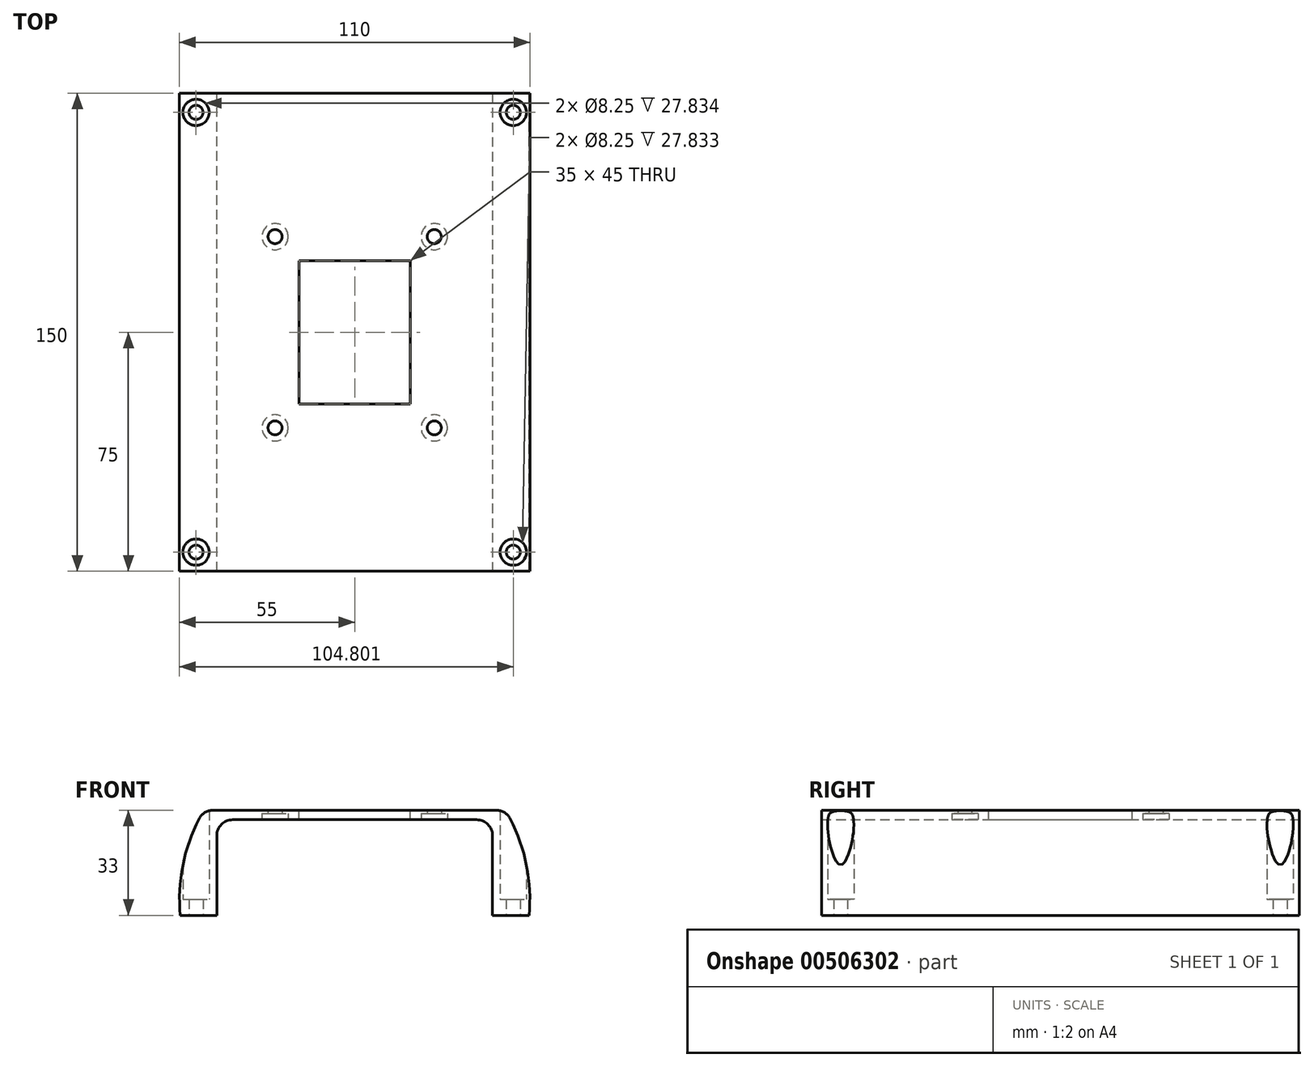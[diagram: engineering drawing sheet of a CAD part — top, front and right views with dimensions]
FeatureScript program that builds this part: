
annotation { "Feature Type Name" : "Feature", "Feature Type Description" : "" }
export const myFeature = defineFeature(function(context is Context, id is Id, definition is map)
    precondition{}
    {
        {
            var Q0;
            Q0=qCreatedBy(makeId("Front.planeOp"),FACE);
            var sketch = newSketch(context, id + "F0", { "sketchPlane" : qUnion([Q0])});
            skCircle(sketch, "E0", {"center": v(0, 0) * mm, "radius": 50 * mm});
            skCircle(sketch, "E1.0", {"center": v(0, 0) * mm, "radius": 55 * mm});
            skSolve(sketch);
        }
        {
            var Q0;
            Q0=qSketchRegion(id+"F0",true);
            extrude(context, id + "F1", {"entities" : qUnion([Q0]), "depth" : 150 * mm});
        }
        {
            var Q0;
            Q0=makeQuery(id+"F1.opExtrude","CAP_FACE",FACE,{"disambiguationData":[OSD([sQuery(id+"F0.wireOp",EDGE,"E0"),sQuery(id+"F0.wireOp",EDGE,"E1.0")])],"isStart":false});
            var sketch = newSketch(context, id + "F2", { "sketchPlane" : qUnion([Q0])});
            skLineSegment(sketch, "E2.bottom", {"start": v(-54.77, -5) * mm, "end": v(54.77, -5) * mm});
            skLineSegment(sketch, "E2.top", {"start": v(-54.08, -10) * mm, "end": v(54.08, -10) * mm});
            skArc(sketch, "E3.0", {"start": v(-54.77, -5) * mm, "mid": v(-54.49, -7.5) * mm, "end": v(-54.08, -10) * mm});
            skArc(sketch, "E4.trimOffspring", {"start": v(54.08, -10) * mm, "mid": v(54.49, -7.5) * mm, "end": v(54.77, -5) * mm});
            skSolve(sketch);
        }
        {
            var Q0;
            Q0=qSketchRegion(id+"F2",true);
            extrude(context, id + "F3", {"entities" : qUnion([Q0]), "operationType" : NewBodyOperationType.ADD, "oppositeDirection" : true, "depth" : 150 * mm});
        }
        {
            var Q0;
            Q0=makeQuery(id+"F3.boolean.opBoolean","MERGE",FACE,{"derivedFrom":[makeQuery(id+"F1.opExtrude","CAP_FACE",FACE,{"disambiguationData":[OSD([sQuery(id+"F0.wireOp",EDGE,"E0"),sQuery(id+"F0.wireOp",EDGE,"E1.0")])],"isStart":false}),makeQuery(id+"F3.opExtrude","CAP_FACE",FACE,{"disambiguationData":[OSD([sQuery(id+"F2.wireOp",EDGE,"E2.bottom"),sQuery(id+"F2.wireOp",EDGE,"E2.top"),sQuery(id+"F2.wireOp",EDGE,"E3.0"),sQuery(id+"F2.wireOp",EDGE,"E4.trimOffspring")])],"isStart":true})]});
            var sketch = newSketch(context, id + "F4", { "sketchPlane" : qUnion([Q0])});
            skLineSegment(sketch, "E5", {"start": v(-48.99, 25) * mm, "end": v(48.99, 25) * mm});
            skLineSegment(sketch, "E6", {"start": v(-47.34, 28) * mm, "end": v(47.34, 28) * mm});
            skArc(sketch, "E7.0", {"start": v(48.99, 25) * mm, "mid": v(48.19, 26.51) * mm, "end": v(47.34, 28) * mm});
            skArc(sketch, "E8.trimOffspring", {"start": v(-47.34, 28) * mm, "mid": v(-48.19, 26.51) * mm, "end": v(-48.99, 25) * mm});
            skSolve(sketch);
        }
        {
            var Q0;
            Q0=qSketchRegion(id+"F4",true);
            extrude(context, id + "F5", {"entities" : qUnion([Q0]), "operationType" : NewBodyOperationType.ADD, "oppositeDirection" : true, "depth" : 150 * mm});
        }
        {
            var Q0;
            Q0=makeQuery(id+"F5.boolean.opBoolean","MERGE",FACE,{"derivedFrom":[makeQuery(id+"F3.boolean.opBoolean","MERGE",FACE,{"derivedFrom":[makeQuery(id+"F1.opExtrude","CAP_FACE",FACE,{"disambiguationData":[OSD([sQuery(id+"F0.wireOp",EDGE,"E0"),sQuery(id+"F0.wireOp",EDGE,"E1.0")])],"isStart":false}),makeQuery(id+"F3.opExtrude","CAP_FACE",FACE,{"disambiguationData":[OSD([sQuery(id+"F2.wireOp",EDGE,"E2.bottom"),sQuery(id+"F2.wireOp",EDGE,"E2.top"),sQuery(id+"F2.wireOp",EDGE,"E3.0"),sQuery(id+"F2.wireOp",EDGE,"E4.trimOffspring")])],"isStart":true})]}),makeQuery(id+"F5.opExtrude","CAP_FACE",FACE,{"disambiguationData":[OSD([sQuery(id+"F4.wireOp",EDGE,"E5"),sQuery(id+"F4.wireOp",EDGE,"E6"),sQuery(id+"F4.wireOp",EDGE,"E7.0"),sQuery(id+"F4.wireOp",EDGE,"E8.trimOffspring")])],"isStart":true})]});
            var sketch = newSketch(context, id + "F6", { "sketchPlane" : qUnion([Q0])});
            skLineSegment(sketch, "E9", {"start": v(-41.42, 28) * mm, "end": v(106.76, 28) * mm});
            skLineSegment(sketch, "E10", {"start": v(106.76, 28) * mm, "end": v(0, 63.47) * mm});
            skLineSegment(sketch, "E11", {"start": v(0, 63.47) * mm, "end": v(-70.4, 28) * mm});
            skLineSegment(sketch, "E12", {"start": v(-70.4, 28) * mm, "end": v(-41.42, 28) * mm});
            skSolve(sketch);
        }
        {
            var Q0;
            Q0=qSketchRegion(id+"F6",true);
            extrude(context, id + "F7", {"entities" : qUnion([Q0]), "operationType" : NewBodyOperationType.REMOVE, "oppositeDirection" : true, "depth" : 233.5 * mm});
        }
        {
            var Q0;
            Q0=makeQuery(id+"F5.boolean.opBoolean","MERGE",FACE,{"derivedFrom":[makeQuery(id+"F3.boolean.opBoolean","MERGE",FACE,{"derivedFrom":[makeQuery(id+"F1.opExtrude","CAP_FACE",FACE,{"disambiguationData":[OSD([sQuery(id+"F0.wireOp",EDGE,"E0"),sQuery(id+"F0.wireOp",EDGE,"E1.0")])],"isStart":false}),makeQuery(id+"F3.opExtrude","CAP_FACE",FACE,{"disambiguationData":[OSD([sQuery(id+"F2.wireOp",EDGE,"E2.bottom"),sQuery(id+"F2.wireOp",EDGE,"E2.top"),sQuery(id+"F2.wireOp",EDGE,"E3.0"),sQuery(id+"F2.wireOp",EDGE,"E4.trimOffspring")])],"isStart":true})]}),makeQuery(id+"F5.opExtrude","CAP_FACE",FACE,{"disambiguationData":[OSD([sQuery(id+"F4.wireOp",EDGE,"E5"),sQuery(id+"F4.wireOp",EDGE,"E6"),sQuery(id+"F4.wireOp",EDGE,"E7.0"),sQuery(id+"F4.wireOp",EDGE,"E8.trimOffspring")])],"isStart":true})]});
            var sketch = newSketch(context, id + "F8", { "sketchPlane" : qUnion([Q0])});
            skLineSegment(sketch, "E13", {"start": v(43.3, 25) * mm, "end": v(43.3, -25) * mm});
            skArc(sketch, "E14.0", {"start": v(43.3, -25) * mm, "mid": v(46.75, -17.73) * mm, "end": v(48.99, -10) * mm});
            skArc(sketch, "E15.0", {"start": v(49.75, -5) * mm, "mid": v(48.88, 10.5) * mm, "end": v(43.3, 25) * mm});
            skPoint(sketch, "E16.orphan", {"position": v(-48.99, -10) * mm});
            skLineSegment(sketch, "E17", {"start": v(49.75, -5) * mm, "end": v(48.99, -10) * mm});
            skLineSegment(sketch, "E18", {"start": v(0, -50) * mm, "end": v(0, -39.73) * mm, "construction": true});
            skPoint(sketch, "E18.endSnap0", {"position": v(0, -50) * mm});
            skLineSegment(sketch, "E19.MirrorCS", {"start": v(-43.3, 25) * mm, "end": v(-43.3, -25) * mm});
            skArc(sketch, "E20.MirrorCS", {"start": v(-43.3, -25) * mm, "mid": v(-46.75, -17.73) * mm, "end": v(-48.99, -10) * mm});
            skLineSegment(sketch, "E21.MirrorCS", {"start": v(-49.75, -5) * mm, "end": v(-48.99, -10) * mm});
            skArc(sketch, "E22.MirrorCS", {"start": v(-49.75, -5) * mm, "mid": v(-48.88, 10.5) * mm, "end": v(-43.3, 25) * mm});
            skSolve(sketch);
        }
        {
            var Q0;
            Q0=qSketchRegion(id+"F8",true);
            extrude(context, id + "F9", {"entities" : qUnion([Q0]), "operationType" : NewBodyOperationType.ADD, "oppositeDirection" : true, "depth" : 150 * mm});
        }
        {
            var Q0;
            Q0=makeQuery(id+"F9.boolean.opBoolean","MERGE",FACE,{"derivedFrom":[makeQuery(id+"F5.boolean.opBoolean","MERGE",FACE,{"derivedFrom":[makeQuery(id+"F3.boolean.opBoolean","MERGE",FACE,{"derivedFrom":[makeQuery(id+"F1.opExtrude","CAP_FACE",FACE,{"disambiguationData":[OSD([sQuery(id+"F0.wireOp",EDGE,"E0"),sQuery(id+"F0.wireOp",EDGE,"E1.0")])],"isStart":false}),makeQuery(id+"F3.opExtrude","CAP_FACE",FACE,{"disambiguationData":[OSD([sQuery(id+"F2.wireOp",EDGE,"E2.bottom"),sQuery(id+"F2.wireOp",EDGE,"E2.top"),sQuery(id+"F2.wireOp",EDGE,"E3.0"),sQuery(id+"F2.wireOp",EDGE,"E4.trimOffspring")])],"isStart":true})]}),makeQuery(id+"F5.opExtrude","CAP_FACE",FACE,{"disambiguationData":[OSD([sQuery(id+"F4.wireOp",EDGE,"E5"),sQuery(id+"F4.wireOp",EDGE,"E6"),sQuery(id+"F4.wireOp",EDGE,"E7.0"),sQuery(id+"F4.wireOp",EDGE,"E8.trimOffspring")])],"isStart":true})]}),makeQuery(id+"F9.opExtrude","CAP_FACE",FACE,{"disambiguationData":[OSD([sQuery(id+"F8.wireOp",EDGE,"E13"),sQuery(id+"F8.wireOp",EDGE,"E14.0"),sQuery(id+"F8.wireOp",EDGE,"E15.0"),sQuery(id+"F8.wireOp",EDGE,"E17")])],"isStart":true}),makeQuery(id+"F9.opExtrude","CAP_FACE",FACE,{"disambiguationData":[OSD([sQuery(id+"F8.wireOp",EDGE,"E19.MirrorCS"),sQuery(id+"F8.wireOp",EDGE,"E20.MirrorCS"),sQuery(id+"F8.wireOp",EDGE,"E21.MirrorCS"),sQuery(id+"F8.wireOp",EDGE,"E22.MirrorCS")])],"isStart":true})]});
            var sketch = newSketch(context, id + "F10", { "sketchPlane" : qUnion([Q0])});
            skLineSegment(sketch, "E23.bottom", {"start": v(15.68, -50.82) * mm, "end": v(-16.53, -50.82) * mm});
            skLineSegment(sketch, "E23.top", {"start": v(15.68, -47.19) * mm, "end": v(-16.53, -47.19) * mm});
            skLineSegment(sketch, "E23.left", {"start": v(15.68, -50.82) * mm, "end": v(15.68, -47.19) * mm});
            skLineSegment(sketch, "E23.right", {"start": v(-16.53, -50.82) * mm, "end": v(-16.53, -47.19) * mm});
            skSolve(sketch);
        }
        {
            var Q0;
            Q0=qSketchRegion(id+"F10",true);
            extrude(context, id + "F11", {"entities" : qUnion([Q0]), "operationType" : NewBodyOperationType.ADD, "oppositeDirection" : true, "depth" : 150 * mm});
        }
        {
            var Q0;
            Q0=makeQuery(id+"F3.opExtrude","SWEPT_FACE",FACE,{"disambiguationData":[OSD([sQuery(id+"F2.wireOp",EDGE,"E2.top")])]});
            cPlane(context, id + "F12", {"entities" : qUnion([Q0]), "cplaneType" : CPlaneType.OFFSET, "offset" : 10 * mm, "width" : 150 * mm, "height" : 150 * mm});
        }
        {
            var Q0;
            Q0=qCreatedBy(id+"F12.planeOp",FACE);
            var sketch = newSketch(context, id + "F13", { "sketchPlane" : qUnion([Q0])});
            skLineSegment(sketch, "E24", {"start": v(49.8, 144) * mm, "end": v(49.8, 4.23) * mm, "construction": true});
            skPoint(sketch, "E25", {"position": v(49.8, 6) * mm});
            skPoint(sketch, "E26", {"position": v(49.8, -57) * mm});
            skPoint(sketch, "E27", {"position": v(49.8, 144) * mm});
            skLineSegment(sketch, "E28", {"start": v(0, 0) * mm, "end": v(0, -24.3) * mm, "construction": true});
            skPoint(sketch, "E29.MirrorP", {"position": v(-49.8, 6) * mm});
            skPoint(sketch, "E30.MirrorP", {"position": v(-49.8, -57) * mm});
            skPoint(sketch, "E31.MirrorP", {"position": v(-49.8, 144) * mm});
            skSolve(sketch);
        }
        {
            var Q0;
            Q0=sQuery(id+"F13.wireOp",VERTEX,"E25");
            var Q1;
            Q1=sQuery(id+"F13.wireOp",VERTEX,"E29.MirrorP");
            var Q2;
            Q2=sQuery(id+"F13.wireOp",VERTEX,"E27");
            var Q3;
            Q3=sQuery(id+"F13.wireOp",VERTEX,"E31.MirrorP");
            var Q4;
            Q4=makeQuery(id+"F1.opExtrude","SWEPT_BODY",BODY,{"disambiguationData":[OSD([sQuery(id+"F0.wireOp",EDGE,"E0"),sQuery(id+"F0.wireOp",EDGE,"E1.0")])]});
            hole(context, id + "F14", {"style" : HoleStyle.C_BORE, "endStyle" : HoleEndStyle.BLIND, "holeDiameter" : 4.4 * mm, "cBoreDiameter" : 8.25 * mm, "cBoreDepth" : 10 * mm, "holeDepth" : 50 * mm, "isTappedThrough" : true, "tappedDepth" : 12 * mm, "tapClearance" : 3, "startFromSketch" : true, "locations" : qUnion([Q0, Q1, Q2, Q3]), "scope" : qUnion([Q4])});
        }
        {
            var Q0;
            Q0=qCreatedBy(id+"F12.planeOp",FACE);
            var sketch = newSketch(context, id + "F15", { "sketchPlane" : qUnion([Q0])});
            skArc(sketch, "E32.0", {"start": v(51.23, 147.87) * mm, "mid": v(45.68, 144) * mm, "end": v(51.23, 140.13) * mm});
            skArc(sketch, "E33.0", {"start": v(51.23, 140.13) * mm, "mid": v(53.93, 144) * mm, "end": v(51.23, 147.87) * mm});
            skArc(sketch, "E34.0", {"start": v(51.23, 2.13) * mm, "mid": v(53.93, 6) * mm, "end": v(51.23, 9.87) * mm});
            skArc(sketch, "E35.0", {"start": v(51.23, 9.87) * mm, "mid": v(45.68, 6) * mm, "end": v(51.23, 2.13) * mm});
            skArc(sketch, "E36.0", {"start": v(-51.23, 140.13) * mm, "mid": v(-45.68, 144) * mm, "end": v(-51.23, 147.87) * mm});
            skArc(sketch, "E37.0", {"start": v(-51.23, 147.87) * mm, "mid": v(-53.93, 144) * mm, "end": v(-51.23, 140.13) * mm});
            skArc(sketch, "E38.0", {"start": v(-51.23, 9.87) * mm, "mid": v(-53.93, 6) * mm, "end": v(-51.23, 2.13) * mm});
            skArc(sketch, "E39.0", {"start": v(-51.23, 2.13) * mm, "mid": v(-45.68, 6) * mm, "end": v(-51.23, 9.87) * mm});
            skSolve(sketch);
        }
        {
            var Q0;
            Q0=qSketchRegion(id+"F15",true);
            extrude(context, id + "F16", {"entities" : qUnion([Q0]), "operationType" : NewBodyOperationType.REMOVE, "oppositeDirection" : true, "depth" : 90.2 * mm, "hasSecondDirection" : true, "secondDirectionOppositeDirection" : true, "secondDirectionDepth" : 15 * mm});
        }
        {
            var Q0;
            Q0=qSketchRegion(id+"F15",true);
            extrude(context, id + "F17", {"entities" : qUnion([Q0]), "operationType" : NewBodyOperationType.REMOVE, "depth" : 25 * mm});
        }
        {
            var Q0;
            Q0=makeQuery(id+"F11.boolean.opBoolean","MERGE",FACE,{"derivedFrom":[makeQuery(id+"F9.boolean.opBoolean","MERGE",FACE,{"derivedFrom":[makeQuery(id+"F5.boolean.opBoolean","MERGE",FACE,{"derivedFrom":[makeQuery(id+"F3.boolean.opBoolean","MERGE",FACE,{"derivedFrom":[makeQuery(id+"F1.opExtrude","CAP_FACE",FACE,{"disambiguationData":[OSD([sQuery(id+"F0.wireOp",EDGE,"E0"),sQuery(id+"F0.wireOp",EDGE,"E1.0")])],"isStart":false}),makeQuery(id+"F3.opExtrude","CAP_FACE",FACE,{"disambiguationData":[OSD([sQuery(id+"F2.wireOp",EDGE,"E2.bottom"),sQuery(id+"F2.wireOp",EDGE,"E2.top"),sQuery(id+"F2.wireOp",EDGE,"E3.0"),sQuery(id+"F2.wireOp",EDGE,"E4.trimOffspring")])],"isStart":true})]}),makeQuery(id+"F5.opExtrude","CAP_FACE",FACE,{"disambiguationData":[OSD([sQuery(id+"F4.wireOp",EDGE,"E5"),sQuery(id+"F4.wireOp",EDGE,"E6"),sQuery(id+"F4.wireOp",EDGE,"E7.0"),sQuery(id+"F4.wireOp",EDGE,"E8.trimOffspring")])],"isStart":true})]}),makeQuery(id+"F9.opExtrude","CAP_FACE",FACE,{"disambiguationData":[OSD([sQuery(id+"F8.wireOp",EDGE,"E13"),sQuery(id+"F8.wireOp",EDGE,"E14.0"),sQuery(id+"F8.wireOp",EDGE,"E15.0"),sQuery(id+"F8.wireOp",EDGE,"E17")])],"isStart":true}),makeQuery(id+"F9.opExtrude","CAP_FACE",FACE,{"disambiguationData":[OSD([sQuery(id+"F8.wireOp",EDGE,"E19.MirrorCS"),sQuery(id+"F8.wireOp",EDGE,"E20.MirrorCS"),sQuery(id+"F8.wireOp",EDGE,"E21.MirrorCS"),sQuery(id+"F8.wireOp",EDGE,"E22.MirrorCS")])],"isStart":true})]}),makeQuery(id+"F11.opExtrude","CAP_FACE",FACE,{"disambiguationData":[OSD([sQuery(id+"F10.wireOp",EDGE,"E23.bottom"),sQuery(id+"F10.wireOp",EDGE,"E23.top"),sQuery(id+"F10.wireOp",EDGE,"E23.left"),sQuery(id+"F10.wireOp",EDGE,"E23.right")])],"isStart":true})]});
            var sketch = newSketch(context, id + "F18", { "sketchPlane" : qUnion([Q0])});
            skLineSegment(sketch, "E40.bottom", {"start": v(-43.3, -5) * mm, "end": v(-83.66, -5) * mm});
            skLineSegment(sketch, "E40.top", {"start": v(-43.3, -61.43) * mm, "end": v(-83.66, -61.43) * mm});
            skLineSegment(sketch, "E40.right", {"start": v(-83.66, -61.43) * mm, "end": v(-83.66, -5) * mm});
            skLineSegment(sketch, "E41.bottom", {"start": v(-43.3, -5) * mm, "end": v(70.57, -5) * mm});
            skLineSegment(sketch, "E41.top", {"start": v(-43.3, -61.43) * mm, "end": v(70.57, -61.43) * mm});
            skLineSegment(sketch, "E41.right", {"start": v(70.57, -61.43) * mm, "end": v(70.57, -5) * mm});
            skSolve(sketch);
        }
        {
            var Q0;
            Q0 = qSketchRegion(id + "F18", true);
            extrude(context, id + "F19", {"entities" : qUnion([Q0]), "operationType" : NewBodyOperationType.REMOVE, "oppositeDirection" : true, "depth" : 274 * mm});
        }
        {
            var Q0;
            Q0=makeQuery(id+"F5.opExtrude","SWEPT_FACE",FACE,{"disambiguationData":[OSD([sQuery(id+"F4.wireOp",EDGE,"E5")])]});
            var sketch = newSketch(context, id + "F20", { "sketchPlane" : qUnion([Q0])});
            skLineSegment(sketch, "E42.bottom", {"start": v(25, 105) * mm, "end": v(-25, 105) * mm, "construction": true});
            skLineSegment(sketch, "E42.top", {"start": v(25, 45) * mm, "end": v(-25, 45) * mm, "construction": true});
            skLineSegment(sketch, "E42.left", {"start": v(25, 105) * mm, "end": v(25, 45) * mm, "construction": true});
            skLineSegment(sketch, "E42.right", {"start": v(-25, 105) * mm, "end": v(-25, 45) * mm, "construction": true});
            skPoint(sketch, "E42.middle", {"position": v(0, 75) * mm});
            skPoint(sketch, "E42.middle.positionSnap0", {"position": v(0, 150) * mm});
            skPoint(sketch, "E42.centerSnap0", {"position": v(0, 150) * mm});
            skSolve(sketch);
        }
        {
            var Q0;
            Q0=sQuery(id+"F20.wireOp",VERTEX,"E42.left.start");
            var Q1;
            Q1=sQuery(id+"F20.wireOp",VERTEX,"E42.left.end");
            var Q2;
            Q2=sQuery(id+"F20.wireOp",VERTEX,"E42.right.end");
            var Q3;
            Q3=sQuery(id+"F20.wireOp",VERTEX,"E42.right.start");
            var Q4;
            Q4=makeQuery(id+"F1.opExtrude","SWEPT_BODY",BODY,{"disambiguationData":[OSD([sQuery(id+"F0.wireOp",EDGE,"E0"),sQuery(id+"F0.wireOp",EDGE,"E1.0")])]});
            hole(context, id + "F21", {"style" : HoleStyle.C_BORE, "endStyle" : HoleEndStyle.BLIND, "holeDiameter" : 4.4 * mm, "cBoreDiameter" : 8.25 * mm, "cBoreDepth" : 2 * mm, "holeDepth" : 50 * mm, "isTappedThrough" : true, "tappedDepth" : 12 * mm, "tapClearance" : 3, "startFromSketch" : true, "locations" : qUnion([Q0, Q1, Q2, Q3]), "scope" : qUnion([Q4])});
        }
        {
            var Q0;
            Q0=makeQuery(id+"F7.boolean.opBoolean","MERGE",FACE,{"derivedFrom":[makeQuery(id+"F5.opExtrude","SWEPT_FACE",FACE,{"disambiguationData":[OSD([sQuery(id+"F4.wireOp",EDGE,"E6")])]}),makeQuery(id+"F7.opExtrude","SWEPT_FACE",FACE,{"disambiguationData":[OSD([sQuery(id+"F6.wireOp",EDGE,"E9"),sQuery(id+"F6.wireOp",EDGE,"E12")])]})]});
            var sketch = newSketch(context, id + "F22", { "sketchPlane" : qUnion([Q0])});
            skLineSegment(sketch, "E43.bottom", {"start": v(-17.5, -52.5) * mm, "end": v(17.5, -52.5) * mm});
            skLineSegment(sketch, "E43.top", {"start": v(-17.5, -97.5) * mm, "end": v(17.5, -97.5) * mm});
            skLineSegment(sketch, "E43.left", {"start": v(-17.5, -52.5) * mm, "end": v(-17.5, -97.5) * mm});
            skLineSegment(sketch, "E43.right", {"start": v(17.5, -52.5) * mm, "end": v(17.5, -97.5) * mm});
            skPoint(sketch, "E43.middle", {"position": v(0, -75) * mm});
            skSolve(sketch);
        }
        {
            var Q0;
            Q0 = qSketchRegion(id + "F22", true);
            extrude(context, id + "F23", {"entities" : qUnion([Q0]), "operationType" : NewBodyOperationType.REMOVE, "oppositeDirection" : true, "depth" : 25 * mm});
        }
        {
            var Q0;
            {var subQ0=makeQuery(id+"F7.opExtrude","SWEPT_FACE",FACE,{"disambiguationData":[OSD([sQuery(id+"F6.wireOp",EDGE,"E9"),sQuery(id+"F6.wireOp",EDGE,"E12")])]});var subQ1=makeQuery(id+"F1.opExtrude","SWEPT_FACE",FACE,{"disambiguationData":[OSD([sQuery(id+"F0.wireOp",EDGE,"E1.0")])]});Q0=makeQuery(id+"F16.boolean.opBoolean","SPLIT",EDGE,{"disambiguationData":[TD([subQ1,makeQuery(id+"F5.opExtrude","SWEPT_FACE",FACE,{"disambiguationData":[OSD([sQuery(id+"F4.wireOp",EDGE,"E6")])]}),subQ0,makeQuery(id+"F16.opExtrude","SWEPT_FACE",FACE,{"disambiguationData":[OSD([sQuery(id+"F15.wireOp",EDGE,"E32.0"),sQuery(id+"F15.wireOp",EDGE,"E33.0")])]}),makeQuery(id+"F16.opExtrude","SWEPT_FACE",FACE,{"disambiguationData":[OSD([sQuery(id+"F15.wireOp",EDGE,"E34.0"),sQuery(id+"F15.wireOp",EDGE,"E35.0")])]})])],"derivedFrom":makeQuery(id+"F7.boolean.opBoolean","INTERSECT",EDGE,{"disambiguationData":[OD(1.0)],"derivedFrom":[subQ1,subQ0]})});}
            var Q1;
            {var subQ0=makeQuery(id+"F7.opExtrude","SWEPT_FACE",FACE,{"disambiguationData":[OSD([sQuery(id+"F6.wireOp",EDGE,"E9"),sQuery(id+"F6.wireOp",EDGE,"E12")])]});var subQ1=makeQuery(id+"F1.opExtrude","SWEPT_FACE",FACE,{"disambiguationData":[OSD([sQuery(id+"F0.wireOp",EDGE,"E1.0")])]});Q1=makeQuery(id+"F16.boolean.opBoolean","SPLIT",EDGE,{"disambiguationData":[TD([subQ1,makeQuery(id+"F5.opExtrude","SWEPT_FACE",FACE,{"disambiguationData":[OSD([sQuery(id+"F4.wireOp",EDGE,"E6")])]}),subQ0,makeQuery(id+"F16.opExtrude","SWEPT_FACE",FACE,{"disambiguationData":[OSD([sQuery(id+"F15.wireOp",EDGE,"E36.0"),sQuery(id+"F15.wireOp",EDGE,"E37.0")])]}),makeQuery(id+"F16.opExtrude","SWEPT_FACE",FACE,{"disambiguationData":[OSD([sQuery(id+"F15.wireOp",EDGE,"E38.0"),sQuery(id+"F15.wireOp",EDGE,"E39.0")])]})])],"derivedFrom":makeQuery(id+"F7.boolean.opBoolean","INTERSECT",EDGE,{"disambiguationData":[OD(0.0)],"derivedFrom":[subQ1,subQ0]})});}
            var Q2;
            {var subQ0=sQuery(id+"F4.wireOp",EDGE,"E5");var subQ4=sQuery(id+"F2.wireOp",EDGE,"E2.bottom");var subQ6=sQuery(id+"F0.wireOp",EDGE,"E0");Q2=makeQuery(id+"F9.boolean.opBoolean","MERGE",EDGE,{"derivedFrom":[makeQuery(id+"F5.boolean.opBoolean","INTERSECT",EDGE,{"disambiguationData":[OD(1.0)],"derivedFrom":[makeQuery(id+"F3.boolean.opBoolean","SPLIT",FACE,{"disambiguationData":[TD([makeQuery(id+"F3.opExtrude","SWEPT_FACE",FACE,{"disambiguationData":[OSD([subQ4])]})])],"derivedFrom":makeQuery(id+"F1.opExtrude","SWEPT_FACE",FACE,{"disambiguationData":[OSD([subQ6])]})}),makeQuery(id+"F5.opExtrude","SWEPT_FACE",FACE,{"disambiguationData":[OSD([subQ0])]})]}),makeQuery(id+"F9.opExtrude","SWEPT_EDGE",EDGE,{"disambiguationData":[OSD([subQ0,sQuery(id+"F8.wireOp",EDGE,"E13"),sQuery(id+"F8.wireOp",EDGE,"E15.0")])]})]});}
            var Q3;
            {var subQ0=sQuery(id+"F4.wireOp",EDGE,"E5");var subQ4=sQuery(id+"F2.wireOp",EDGE,"E2.bottom");var subQ6=sQuery(id+"F0.wireOp",EDGE,"E0");Q3=makeQuery(id+"F9.boolean.opBoolean","MERGE",EDGE,{"derivedFrom":[makeQuery(id+"F5.boolean.opBoolean","INTERSECT",EDGE,{"disambiguationData":[OD(0.0)],"derivedFrom":[makeQuery(id+"F3.boolean.opBoolean","SPLIT",FACE,{"disambiguationData":[TD([makeQuery(id+"F3.opExtrude","SWEPT_FACE",FACE,{"disambiguationData":[OSD([subQ4])]})])],"derivedFrom":makeQuery(id+"F1.opExtrude","SWEPT_FACE",FACE,{"disambiguationData":[OSD([subQ6])]})}),makeQuery(id+"F5.opExtrude","SWEPT_FACE",FACE,{"disambiguationData":[OSD([subQ0])]})]}),makeQuery(id+"F9.opExtrude","SWEPT_EDGE",EDGE,{"disambiguationData":[OSD([subQ0,sQuery(id+"F8.wireOp",EDGE,"E19.MirrorCS"),sQuery(id+"F8.wireOp",EDGE,"E22.MirrorCS")])]})]});}
            fillet(context, id + "F24", {"entities" : qUnion([Q0, Q1, Q2, Q3]), "radius" : 5 * mm, "tangentPropagation" : true, "allowEdgeOverflow" : false});
        }
        {
            var Q0;
            {var subQ0=sQuery(id+"F8.wireOp",EDGE,"E19.MirrorCS");Q0=makeQuery(id+"F19.boolean.opBoolean","COPY",FACE,{"disambiguationData":[TD([makeQuery(id+"F9.opExtrude","SWEPT_FACE",FACE,{"disambiguationData":[OSD([subQ0])]})])],"derivedFrom":makeQuery(id+"F19.opExtrude","SWEPT_FACE",FACE,{"disambiguationData":[OSD([sQuery(id+"F18.wireOp",EDGE,"E40.bottom"),sQuery(id+"F18.wireOp",EDGE,"E41.bottom")])]})});}
            var sketch = newSketch(context, id + "F25", { "sketchPlane" : qUnion([Q0])});
            skCircle(sketch, "E44.0", {"center": v(-49.8, 144) * mm, "radius": 4.12 * mm});
            skCircle(sketch, "E45.0", {"center": v(49.8, 144) * mm, "radius": 4.12 * mm});
            skCircle(sketch, "E46.0", {"center": v(49.8, 6) * mm, "radius": 4.12 * mm});
            skCircle(sketch, "E47.0", {"center": v(-49.8, 6) * mm, "radius": 4.12 * mm});
            skCircle(sketch, "E48", {"center": v(-49.8, 144) * mm, "radius": 2.2 * mm});
            skCircle(sketch, "E49", {"center": v(49.8, 144) * mm, "radius": 2.2 * mm});
            skCircle(sketch, "E50", {"center": v(-49.8, 6) * mm, "radius": 2.2 * mm});
            skCircle(sketch, "E51", {"center": v(49.8, 6) * mm, "radius": 2.2 * mm});
            skSolve(sketch);
        }
        {
            var Q0;
            Q0 = qSketchRegion(id + "F25", true);
            extrude(context, id + "F26", {"entities" : qUnion([Q0]), "operationType" : NewBodyOperationType.ADD, "oppositeDirection" : true, "depth" : 5 * mm, "offsetDistance" : 25 * mm});
        }
    });
